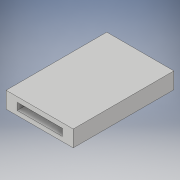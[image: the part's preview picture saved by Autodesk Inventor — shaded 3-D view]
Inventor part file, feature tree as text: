
AUTODESK INVENTOR PART (.ipt)
format: ipt  version: 2019 (Build 230136000, 136)  size: 96,256 bytes
history: native  units: mm
features: extrude x2, sketch x2
ambient origin geometry x8: Origin, YZ Plane, XZ Plane, XY Plane, X Axis, Y Axis, Z Axis, Center Point
bodies: Solid1 (feature_tree)
feature tree (4):
  extrude  "Extrusion1"  Depth=15.0mm TaperAngle=0.0deg
  extrude  "Extrusion2"  [1 undecoded]
  sketch  "Sketch1"  dims[d0=10.0mm d1=15.0mm d2=0.0mm]
  sketch  "Sketch2"  dims[d3=1.5mm d4=0.0mm]
note: 1 required parameter value undecoded (feature->parameter linkage not recoverable at this tier; creation-order binding heuristic only, values carry confidence <= 0.55)
